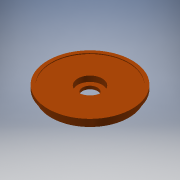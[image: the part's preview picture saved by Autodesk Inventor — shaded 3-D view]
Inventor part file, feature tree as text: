
AUTODESK INVENTOR PART (.ipt)
format: ipt  version: 2017 SP1 (Build 210196100, 196)  size: 150,016 bytes
history: native  units: in
note: dims shown in document units (in); Inventor stores cm internally (conversion verified against a paired STEP export)
features: revolve x1, sketch x1
ambient origin geometry x8: Origin, YZ Plane, XZ Plane, XY Plane, X Axis, Y Axis, Z Axis, Center Point
bodies: Body1 (feature_tree)
feature tree (2):
  revolve  "Revolution2"  [1 undecoded]
  sketch  "Sketch1"  dims[d0=2.5935in d1=0.375in d7=0.1in d8=0.088in d9=0.275in d24=0.368in d25=0.207in d26=0.315in d27=0.5in d28=0.207in d30=0.2338in d32=0.25in d33=0.05in d34=1.7637in d35=90.0deg]
note: 1 required parameter value undecoded (feature->parameter linkage not recoverable at this tier; creation-order binding heuristic only, values carry confidence <= 0.55)
